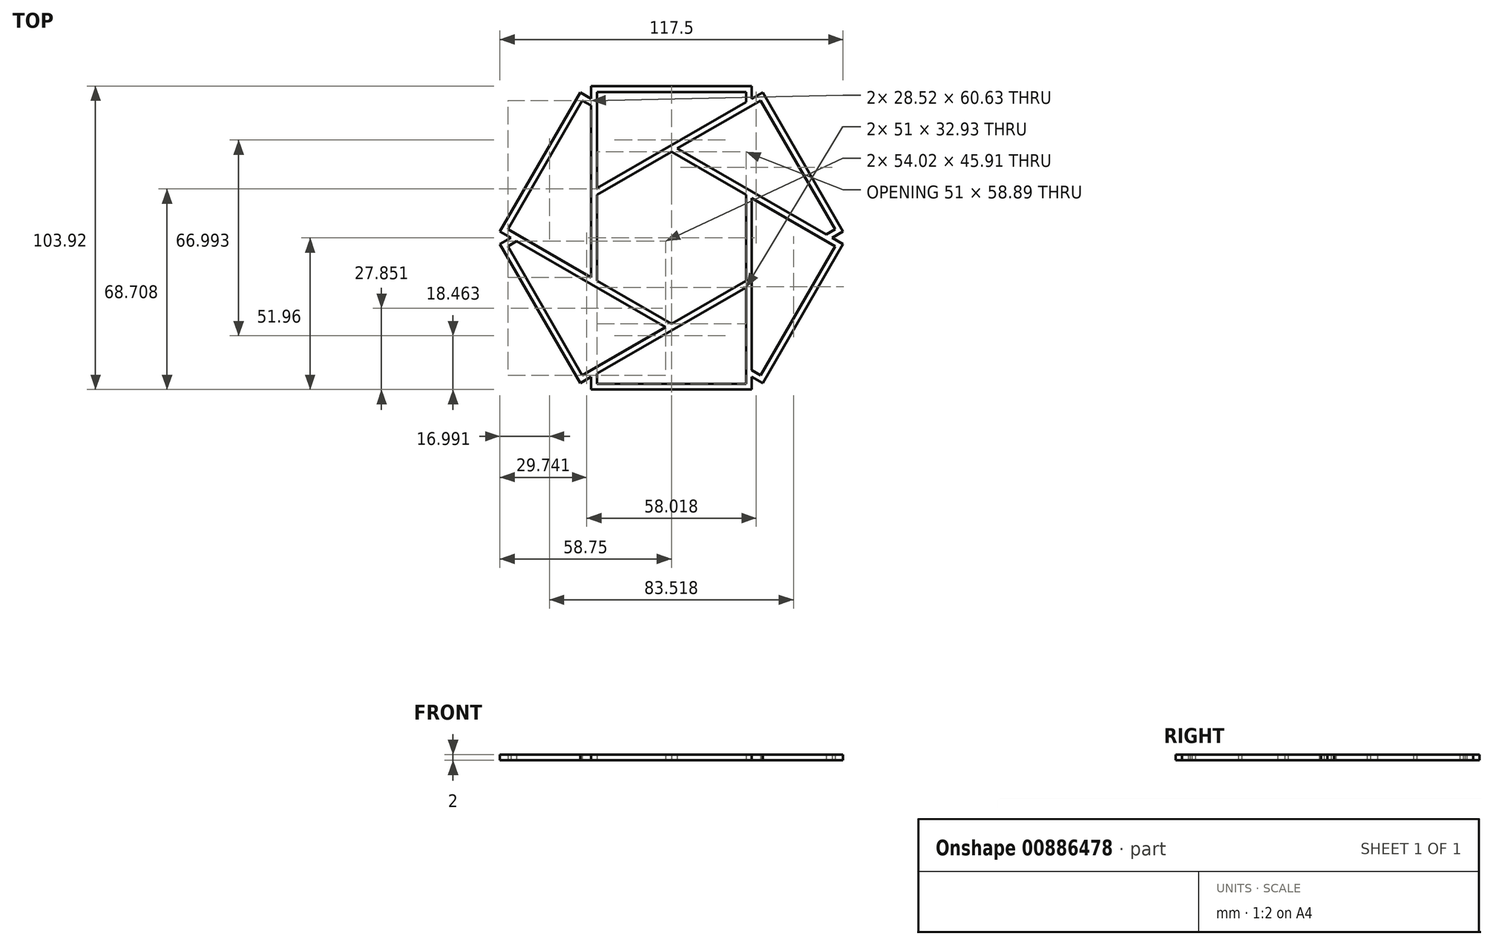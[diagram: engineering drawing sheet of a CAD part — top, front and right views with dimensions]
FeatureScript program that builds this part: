
annotation { "Feature Type Name" : "Feature", "Feature Type Description" : "" }
export const myFeature = defineFeature(function(context is Context, id is Id, definition is map)
    precondition{}
    {
        {
            var Q0;
            Q0=qCreatedBy(makeId("Top.planeOp"),FACE);
            var sketch = newSketch(context, id + "F0", { "sketchPlane" : qUnion([Q0])});
            skCircle(sketch, "E0.cCircle", {"center": v(0, 0) * mm, "radius": 60 * mm, "construction": true});
            skLineSegment(sketch, "E0.0", {"start": v(-60, 0) * mm, "end": v(-30, 51.96) * mm, "construction": true});
            skLineSegment(sketch, "E0.1", {"start": v(-30, 51.96) * mm, "end": v(30, 51.96) * mm, "construction": true});
            skLineSegment(sketch, "E0.2", {"start": v(30, 51.96) * mm, "end": v(60, 0) * mm, "construction": true});
            skLineSegment(sketch, "E0.3", {"start": v(60, 0) * mm, "end": v(30, -51.96) * mm, "construction": true});
            skLineSegment(sketch, "E0.4", {"start": v(30, -51.96) * mm, "end": v(-30, -51.96) * mm, "construction": true});
            skLineSegment(sketch, "E0.5", {"start": v(-30, -51.96) * mm, "end": v(-60, 0) * mm, "construction": true});
            skLineSegment(sketch, "E1.bottom", {"start": v(-27.5, 51.96) * mm, "end": v(27.5, 51.96) * mm});
            skLineSegment(sketch, "E1.top", {"start": v(-27.5, -51.96) * mm, "end": v(27.5, -51.96) * mm});
            skLineSegment(sketch, "E1.left", {"start": v(-27.5, 51.96) * mm, "end": v(-27.5, -15.88) * mm});
            skLineSegment(sketch, "E1.right", {"start": v(27.5, 51.96) * mm, "end": v(27.5, 45.32) * mm});
            skLineSegment(sketch, "E2.0", {"start": v(-25.5, -49.96) * mm, "end": v(25.5, -49.96) * mm});
            skLineSegment(sketch, "E2.1", {"start": v(-25.5, 49.96) * mm, "end": v(-25.5, -17.03) * mm});
            skLineSegment(sketch, "E2.2", {"start": v(-25.5, 49.96) * mm, "end": v(25.5, 49.96) * mm});
            skLineSegment(sketch, "E2.3", {"start": v(25.5, 49.96) * mm, "end": v(25.5, 44.17) * mm});
            skLineSegment(sketch, "E3.1.0", {"start": v(-30.52, -47.06) * mm, "end": v(27.5, -13.57) * mm});
            skLineSegment(sketch, "E3.1.1", {"start": v(58.75, 2.17) * mm, "end": v(31.25, 49.8) * mm});
            skLineSegment(sketch, "E3.1.2", {"start": v(-31.25, -49.8) * mm, "end": v(-58.75, -2.17) * mm});
            skLineSegment(sketch, "E3.1.3", {"start": v(-30.52, -47.06) * mm, "end": v(-56.02, -2.9) * mm});
            skLineSegment(sketch, "E3.1.4", {"start": v(-56.02, -2.9) * mm, "end": v(-51, 0) * mm});
            skLineSegment(sketch, "E3.1.5", {"start": v(-58.75, -2.17) * mm, "end": v(-53, 1.15) * mm});
            skLineSegment(sketch, "E3.1.7", {"start": v(56.02, 2.9) * mm, "end": v(30.52, 47.06) * mm});
            skLineSegment(sketch, "E3.1.8", {"start": v(-31.25, -49.8) * mm, "end": v(27.5, -15.88) * mm});
            skLineSegment(sketch, "E3.2.0", {"start": v(56.02, -2.9) * mm, "end": v(-2, 30.6) * mm});
            skLineSegment(sketch, "E3.2.1", {"start": v(-31.25, 49.8) * mm, "end": v(-58.75, 2.17) * mm});
            skLineSegment(sketch, "E3.2.2", {"start": v(58.75, -2.17) * mm, "end": v(31.25, -49.8) * mm});
            skLineSegment(sketch, "E3.2.3", {"start": v(56.02, -2.9) * mm, "end": v(30.52, -47.06) * mm});
            skLineSegment(sketch, "E3.2.4", {"start": v(30.52, -47.06) * mm, "end": v(25.5, -44.17) * mm});
            skLineSegment(sketch, "E3.2.5", {"start": v(31.25, -49.8) * mm, "end": v(25.5, -46.48) * mm});
            skLineSegment(sketch, "E3.2.7", {"start": v(-30.52, 47.06) * mm, "end": v(-56.02, 2.9) * mm});
            skLineSegment(sketch, "E3.2.8", {"start": v(58.75, -2.17) * mm, "end": v(0, 31.75) * mm});
            skLineSegment(sketch, "E4.trimOffspring", {"start": v(-25.5, 44.17) * mm, "end": v(-30.52, 47.06) * mm});
            skLineSegment(sketch, "E5.trimOffspring", {"start": v(-25.5, 46.48) * mm, "end": v(-31.25, 49.8) * mm});
            skLineSegment(sketch, "E6.trimOffspring", {"start": v(-27.5, 15.88) * mm, "end": v(31.25, 49.8) * mm});
            skLineSegment(sketch, "E7.trimOffspring", {"start": v(-27.5, 13.57) * mm, "end": v(30.52, 47.06) * mm});
            skLineSegment(sketch, "E8.trimOffspring", {"start": v(-27.5, -45.32) * mm, "end": v(-27.5, -51.96) * mm});
            skLineSegment(sketch, "E9.trimOffspring", {"start": v(-25.5, -44.17) * mm, "end": v(-25.5, -49.96) * mm});
            skLineSegment(sketch, "E10.trimOffspring", {"start": v(0, -31.75) * mm, "end": v(-58.75, 2.17) * mm});
            skLineSegment(sketch, "E11.trimOffspring", {"start": v(2, -30.6) * mm, "end": v(-56.02, 2.9) * mm});
            skLineSegment(sketch, "E12.trimOffspring", {"start": v(51, 0) * mm, "end": v(56.02, 2.9) * mm});
            skLineSegment(sketch, "E13.trimOffspring", {"start": v(53, -1.15) * mm, "end": v(58.75, 2.17) * mm});
            skLineSegment(sketch, "E14.trimOffspring", {"start": v(27.5, 15.88) * mm, "end": v(27.5, -51.96) * mm});
            skLineSegment(sketch, "E15.trimOffspring", {"start": v(25.5, 17.03) * mm, "end": v(25.5, -49.96) * mm});
            skSolve(sketch);
        }
        {
            var Q0;
            {var subQ0=sQuery(id+"F0.wireOp",EDGE,"E3.1.4");var subQ1=sQuery(id+"F0.wireOp",EDGE,"E1.left");var subQ2=makeQuery(id+"F0.imprint","INTERSECT",VERTEX,{"derivedFrom":[subQ1,subQ0]});Q0=makeQuery(id+"F0.imprint","IMPRINT",FACE,{"disambiguationData":[TD([[makeQuery(id+"F0.imprint","IMPRINT",EDGE,{"disambiguationData":[TD([[subQ2,-1.0]])],"derivedFrom":subQ1}),1.0]])]});}
            var Q1;
            {var subQ0=sQuery(id+"F0.wireOp",EDGE,"E3.2.4");var subQ1=sQuery(id+"F0.wireOp",EDGE,"E1.left");var subQ2=makeQuery(id+"F0.imprint","INTERSECT",VERTEX,{"derivedFrom":[subQ1,subQ0]});Q1=makeQuery(id+"F0.imprint","IMPRINT",FACE,{"disambiguationData":[TD([[makeQuery(id+"F0.imprint","IMPRINT",EDGE,{"disambiguationData":[TD([[subQ2,-1.0]])],"derivedFrom":subQ1}),1.0]])]});}
            var Q2;
            {var subQ0=sQuery(id+"F0.wireOp",EDGE,"E3.2.5");var subQ1=sQuery(id+"F0.wireOp",EDGE,"E1.left");var subQ2=makeQuery(id+"F0.imprint","INTERSECT",VERTEX,{"derivedFrom":[subQ1,subQ0]});Q2=makeQuery(id+"F0.imprint","IMPRINT",FACE,{"disambiguationData":[TD([[makeQuery(id+"F0.imprint","IMPRINT",EDGE,{"disambiguationData":[TD([[subQ2,-1.0]])],"derivedFrom":subQ1}),1.0]])]});}
            var Q3;
            {var subQ0=sQuery(id+"F0.wireOp",EDGE,"E3.1.8");var subQ1=sQuery(id+"F0.wireOp",EDGE,"E1.left");var subQ2=makeQuery(id+"F0.imprint","INTERSECT",VERTEX,{"derivedFrom":[subQ1,subQ0]});Q3=makeQuery(id+"F0.imprint","IMPRINT",FACE,{"disambiguationData":[TD([[makeQuery(id+"F0.imprint","IMPRINT",EDGE,{"disambiguationData":[TD([[subQ2,1.0]])],"derivedFrom":subQ1}),1.0]])]});}
            var Q4;
            {var subQ4=sQuery(id+"F0.wireOp",EDGE,"E3.1.2");Q4=makeQuery(id+"F0.imprint","IMPRINT",FACE,{"disambiguationData":[TD([[makeQuery(id+"F0.imprint","IMPRINT",EDGE,{"derivedFrom":subQ4}),-1.0]])]});}
            var Q5;
            {var subQ1=sQuery(id+"F0.wireOp",EDGE,"E1.top");Q5=makeQuery(id+"F0.imprint","IMPRINT",FACE,{"disambiguationData":[TD([[makeQuery(id+"F0.imprint","IMPRINT",EDGE,{"derivedFrom":subQ1}),1.0]])]});}
            var Q6;
            {var subQ0=sQuery(id+"F0.wireOp",EDGE,"E3.2.4");var subQ1=sQuery(id+"F0.wireOp",EDGE,"E2.3");var subQ2=makeQuery(id+"F0.imprint","INTERSECT",VERTEX,{"derivedFrom":[subQ1,subQ0]});Q6=makeQuery(id+"F0.imprint","IMPRINT",FACE,{"disambiguationData":[TD([[makeQuery(id+"F0.imprint","IMPRINT",EDGE,{"disambiguationData":[TD([[subQ2,-1.0]])],"derivedFrom":subQ1}),-1.0]])]});}
            var Q7;
            {var subQ0=sQuery(id+"F0.wireOp",EDGE,"E3.2.5");var subQ1=sQuery(id+"F0.wireOp",EDGE,"E1.right");var subQ2=makeQuery(id+"F0.imprint","INTERSECT",VERTEX,{"derivedFrom":[subQ1,subQ0]});Q7=makeQuery(id+"F0.imprint","IMPRINT",FACE,{"disambiguationData":[TD([[makeQuery(id+"F0.imprint","IMPRINT",EDGE,{"disambiguationData":[TD([[subQ2,1.0]])],"derivedFrom":subQ1}),-1.0]])]});}
            var Q8;
            {var subQ0=sQuery(id+"F0.wireOp",EDGE,"E3.2.5");var subQ1=sQuery(id+"F0.wireOp",EDGE,"E3.1.0");var subQ2=makeQuery(id+"F0.imprint","INTERSECT",VERTEX,{"derivedFrom":[subQ1,subQ0]});Q8=makeQuery(id+"F0.imprint","IMPRINT",FACE,{"disambiguationData":[TD([[makeQuery(id+"F0.imprint","IMPRINT",EDGE,{"disambiguationData":[TD([[subQ2,-1.0]])],"derivedFrom":subQ1}),-1.0]])]});}
            var Q9;
            {var subQ0=sQuery(id+"F0.wireOp",EDGE,"E3.1.0");var subQ1=sQuery(id+"F0.wireOp",EDGE,"E2.3");var subQ2=makeQuery(id+"F0.imprint","INTERSECT",VERTEX,{"derivedFrom":[subQ1,subQ0]});Q9=makeQuery(id+"F0.imprint","IMPRINT",FACE,{"disambiguationData":[TD([[makeQuery(id+"F0.imprint","IMPRINT",EDGE,{"disambiguationData":[TD([[subQ2,-1.0]])],"derivedFrom":subQ1}),-1.0]])]});}
            var Q10;
            {var subQ0=sQuery(id+"F0.wireOp",EDGE,"E3.1.8");var subQ1=sQuery(id+"F0.wireOp",EDGE,"E1.right");var subQ2=makeQuery(id+"F0.imprint","INTERSECT",VERTEX,{"derivedFrom":[subQ1,subQ0]});Q10=makeQuery(id+"F0.imprint","IMPRINT",FACE,{"disambiguationData":[TD([[makeQuery(id+"F0.imprint","IMPRINT",EDGE,{"disambiguationData":[TD([[subQ2,-1.0]])],"derivedFrom":subQ1}),-1.0]])]});}
            var Q11;
            {var subQ0=sQuery(id+"F0.wireOp",EDGE,"E3.1.0");var subQ1=sQuery(id+"F0.wireOp",EDGE,"E1.right");var subQ2=makeQuery(id+"F0.imprint","INTERSECT",VERTEX,{"derivedFrom":[subQ1,subQ0]});Q11=makeQuery(id+"F0.imprint","IMPRINT",FACE,{"disambiguationData":[TD([[makeQuery(id+"F0.imprint","IMPRINT",EDGE,{"disambiguationData":[TD([[subQ2,-1.0]])],"derivedFrom":subQ1}),-1.0]])]});}
            var Q12;
            {var subQ0=sQuery(id+"F0.wireOp",EDGE,"E3.2.2");Q12=makeQuery(id+"F0.imprint","IMPRINT",FACE,{"disambiguationData":[TD([[makeQuery(id+"F0.imprint","IMPRINT",EDGE,{"derivedFrom":subQ0}),-1.0]])]});}
            var Q13;
            {var subQ0=sQuery(id+"F0.wireOp",EDGE,"E3.1.0");var subQ1=sQuery(id+"F0.wireOp",EDGE,"E1.right");var subQ2=makeQuery(id+"F0.imprint","INTERSECT",VERTEX,{"derivedFrom":[subQ1,subQ0]});Q13=makeQuery(id+"F0.imprint","IMPRINT",FACE,{"disambiguationData":[TD([[makeQuery(id+"F0.imprint","IMPRINT",EDGE,{"disambiguationData":[TD([[subQ2,-1.0]])],"derivedFrom":subQ1}),1.0]])]});}
            var Q14;
            {var subQ0=sQuery(id+"F0.wireOp",EDGE,"E3.2.5");var subQ1=sQuery(id+"F0.wireOp",EDGE,"E3.1.4");var subQ2=makeQuery(id+"F0.imprint","INTERSECT",VERTEX,{"derivedFrom":[subQ1,subQ0]});Q14=makeQuery(id+"F0.imprint","IMPRINT",FACE,{"disambiguationData":[TD([[makeQuery(id+"F0.imprint","IMPRINT",EDGE,{"disambiguationData":[TD([[subQ2,-1.0]])],"derivedFrom":subQ1}),1.0]])]});}
            var Q15;
            {var subQ0=sQuery(id+"F0.wireOp",EDGE,"E3.2.1");Q15=makeQuery(id+"F0.imprint","IMPRINT",FACE,{"disambiguationData":[TD([[makeQuery(id+"F0.imprint","IMPRINT",EDGE,{"derivedFrom":subQ0}),1.0]])]});}
            var Q16;
            {var subQ0=sQuery(id+"F0.wireOp",EDGE,"E3.2.0");var subQ1=sQuery(id+"F0.wireOp",EDGE,"E1.left");var subQ2=makeQuery(id+"F0.imprint","INTERSECT",VERTEX,{"derivedFrom":[subQ1,subQ0]});Q16=makeQuery(id+"F0.imprint","IMPRINT",FACE,{"disambiguationData":[TD([[makeQuery(id+"F0.imprint","IMPRINT",EDGE,{"disambiguationData":[TD([[subQ2,-1.0]])],"derivedFrom":subQ1}),1.0]])]});}
            var Q17;
            {var subQ0=sQuery(id+"F0.wireOp",EDGE,"E3.1.5");var subQ1=sQuery(id+"F0.wireOp",EDGE,"E1.left");var subQ2=makeQuery(id+"F0.imprint","INTERSECT",VERTEX,{"derivedFrom":[subQ1,subQ0]});Q17=makeQuery(id+"F0.imprint","IMPRINT",FACE,{"disambiguationData":[TD([[makeQuery(id+"F0.imprint","IMPRINT",EDGE,{"disambiguationData":[TD([[subQ2,-1.0]])],"derivedFrom":subQ1}),1.0]])]});}
            var Q18;
            {var subQ0=sQuery(id+"F0.wireOp",EDGE,"E3.2.8");var subQ1=sQuery(id+"F0.wireOp",EDGE,"E1.left");var subQ2=makeQuery(id+"F0.imprint","INTERSECT",VERTEX,{"derivedFrom":[subQ1,subQ0]});Q18=makeQuery(id+"F0.imprint","IMPRINT",FACE,{"disambiguationData":[TD([[makeQuery(id+"F0.imprint","IMPRINT",EDGE,{"disambiguationData":[TD([[subQ2,-1.0]])],"derivedFrom":subQ1}),1.0]])]});}
            var Q19;
            {var subQ5=sQuery(id+"F0.wireOp",EDGE,"E1.bottom");Q19=makeQuery(id+"F0.imprint","IMPRINT",FACE,{"disambiguationData":[TD([[makeQuery(id+"F0.imprint","IMPRINT",EDGE,{"derivedFrom":subQ5}),-1.0]])]});}
            var Q20;
            {var subQ0=sQuery(id+"F0.wireOp",EDGE,"E3.2.0");var subQ1=sQuery(id+"F0.wireOp",EDGE,"E3.1.4");var subQ2=makeQuery(id+"F0.imprint","INTERSECT",VERTEX,{"derivedFrom":[subQ1,subQ0]});Q20=makeQuery(id+"F0.imprint","IMPRINT",FACE,{"disambiguationData":[TD([[makeQuery(id+"F0.imprint","IMPRINT",EDGE,{"disambiguationData":[TD([[subQ2,-1.0]])],"derivedFrom":subQ1}),1.0]])]});}
            var Q21;
            {var subQ0=sQuery(id+"F0.wireOp",EDGE,"E3.1.5");var subQ1=sQuery(id+"F0.wireOp",EDGE,"E2.3");var subQ2=makeQuery(id+"F0.imprint","INTERSECT",VERTEX,{"derivedFrom":[subQ1,subQ0]});Q21=makeQuery(id+"F0.imprint","IMPRINT",FACE,{"disambiguationData":[TD([[makeQuery(id+"F0.imprint","IMPRINT",EDGE,{"disambiguationData":[TD([[subQ2,-1.0]])],"derivedFrom":subQ1}),-1.0]])]});}
            var Q22;
            {var subQ0=sQuery(id+"F0.wireOp",EDGE,"E3.2.8");var subQ1=sQuery(id+"F0.wireOp",EDGE,"E2.3");var subQ2=makeQuery(id+"F0.imprint","INTERSECT",VERTEX,{"derivedFrom":[subQ1,subQ0]});Q22=makeQuery(id+"F0.imprint","IMPRINT",FACE,{"disambiguationData":[TD([[makeQuery(id+"F0.imprint","IMPRINT",EDGE,{"disambiguationData":[TD([[subQ2,-1.0]])],"derivedFrom":subQ1}),-1.0]])]});}
            var Q23;
            {var subQ0=sQuery(id+"F0.wireOp",EDGE,"E3.1.4");var subQ1=sQuery(id+"F0.wireOp",EDGE,"E1.right");var subQ2=makeQuery(id+"F0.imprint","INTERSECT",VERTEX,{"derivedFrom":[subQ1,subQ0]});Q23=makeQuery(id+"F0.imprint","IMPRINT",FACE,{"disambiguationData":[TD([[makeQuery(id+"F0.imprint","IMPRINT",EDGE,{"disambiguationData":[TD([[subQ2,-1.0]])],"derivedFrom":subQ1}),-1.0]])]});}
            var Q24;
            {var subQ0=sQuery(id+"F0.wireOp",EDGE,"E3.1.5");var subQ1=sQuery(id+"F0.wireOp",EDGE,"E1.right");var subQ2=makeQuery(id+"F0.imprint","INTERSECT",VERTEX,{"derivedFrom":[subQ1,subQ0]});Q24=makeQuery(id+"F0.imprint","IMPRINT",FACE,{"disambiguationData":[TD([[makeQuery(id+"F0.imprint","IMPRINT",EDGE,{"disambiguationData":[TD([[subQ2,-1.0]])],"derivedFrom":subQ1}),-1.0]])]});}
            var Q25;
            {var subQ4=sQuery(id+"F0.wireOp",EDGE,"E3.1.1");Q25=makeQuery(id+"F0.imprint","IMPRINT",FACE,{"disambiguationData":[TD([[makeQuery(id+"F0.imprint","IMPRINT",EDGE,{"derivedFrom":subQ4}),1.0]])]});}
            var Q26;
            {var subQ0=sQuery(id+"F0.wireOp",EDGE,"E3.2.8");var subQ1=sQuery(id+"F0.wireOp",EDGE,"E1.right");var subQ2=makeQuery(id+"F0.imprint","INTERSECT",VERTEX,{"derivedFrom":[subQ1,subQ0]});Q26=makeQuery(id+"F0.imprint","IMPRINT",FACE,{"disambiguationData":[TD([[makeQuery(id+"F0.imprint","IMPRINT",EDGE,{"disambiguationData":[TD([[subQ2,-1.0]])],"derivedFrom":subQ1}),-1.0]])]});}
            var Q27;
            {var subQ0=sQuery(id+"F0.wireOp",EDGE,"E3.2.0");var subQ1=sQuery(id+"F0.wireOp",EDGE,"E1.right");var subQ2=makeQuery(id+"F0.imprint","INTERSECT",VERTEX,{"derivedFrom":[subQ1,subQ0]});Q27=makeQuery(id+"F0.imprint","IMPRINT",FACE,{"disambiguationData":[TD([[makeQuery(id+"F0.imprint","IMPRINT",EDGE,{"disambiguationData":[TD([[subQ2,-1.0]])],"derivedFrom":subQ1}),-1.0]])]});}
            var Q28;
            {var subQ0=sQuery(id+"F0.wireOp",EDGE,"E3.2.8");var subQ1=sQuery(id+"F0.wireOp",EDGE,"E1.right");var subQ2=makeQuery(id+"F0.imprint","INTERSECT",VERTEX,{"derivedFrom":[subQ1,subQ0]});Q28=makeQuery(id+"F0.imprint","IMPRINT",FACE,{"disambiguationData":[TD([[makeQuery(id+"F0.imprint","IMPRINT",EDGE,{"disambiguationData":[TD([[subQ2,-1.0]])],"derivedFrom":subQ1}),1.0]])]});}
            var Q29;
            {var subQ0=sQuery(id+"F0.wireOp",EDGE,"E3.2.0");var subQ1=sQuery(id+"F0.wireOp",EDGE,"E3.1.0");var subQ2=makeQuery(id+"F0.imprint","INTERSECT",VERTEX,{"derivedFrom":[subQ1,subQ0]});Q29=makeQuery(id+"F0.imprint","IMPRINT",FACE,{"disambiguationData":[TD([[makeQuery(id+"F0.imprint","IMPRINT",EDGE,{"disambiguationData":[TD([[subQ2,-1.0]])],"derivedFrom":subQ1}),-1.0]])]});}
            var Q30;
            {var subQ0=sQuery(id+"F0.wireOp",EDGE,"E6.trimOffspring");var subQ1=sQuery(id+"F0.wireOp",EDGE,"E2.1");var subQ2=makeQuery(id+"F0.imprint","INTERSECT",VERTEX,{"derivedFrom":[subQ1,subQ0]});Q30=makeQuery(id+"F0.imprint","IMPRINT",FACE,{"disambiguationData":[TD([[makeQuery(id+"F0.imprint","IMPRINT",EDGE,{"disambiguationData":[TD([[subQ2,-1.0]])],"derivedFrom":subQ1}),1.0]])]});}
            var Q31;
            {var subQ0=sQuery(id+"F0.wireOp",EDGE,"E6.trimOffspring");var subQ1=sQuery(id+"F0.wireOp",EDGE,"E3.2.0");var subQ2=makeQuery(id+"F0.imprint","INTERSECT",VERTEX,{"derivedFrom":[subQ1,subQ0]});Q31=makeQuery(id+"F0.imprint","IMPRINT",FACE,{"disambiguationData":[TD([[makeQuery(id+"F0.imprint","IMPRINT",EDGE,{"disambiguationData":[TD([[subQ2,1.0]])],"derivedFrom":subQ1}),-1.0]])]});}
            var Q32;
            {var subQ0=sQuery(id+"F0.wireOp",EDGE,"E12.trimOffspring");var subQ1=sQuery(id+"F0.wireOp",EDGE,"E3.2.0");var subQ2=makeQuery(id+"F0.imprint","INTERSECT",VERTEX,{"derivedFrom":[subQ1,subQ0]});Q32=makeQuery(id+"F0.imprint","IMPRINT",FACE,{"disambiguationData":[TD([[makeQuery(id+"F0.imprint","IMPRINT",EDGE,{"disambiguationData":[TD([[subQ2,1.0]])],"derivedFrom":subQ1}),-1.0]])]});}
            var Q33;
            {var subQ0=sQuery(id+"F0.wireOp",EDGE,"E10.trimOffspring");var subQ1=sQuery(id+"F0.wireOp",EDGE,"E1.left");var subQ2=makeQuery(id+"F0.imprint","INTERSECT",VERTEX,{"derivedFrom":[subQ1,subQ0]});Q33=makeQuery(id+"F0.imprint","IMPRINT",FACE,{"disambiguationData":[TD([[makeQuery(id+"F0.imprint","IMPRINT",EDGE,{"disambiguationData":[TD([[subQ2,1.0]])],"derivedFrom":subQ1}),-1.0]])]});}
            var Q34;
            {var subQ0=sQuery(id+"F0.wireOp",EDGE,"E10.trimOffspring");var subQ1=sQuery(id+"F0.wireOp",EDGE,"E2.1");var subQ2=makeQuery(id+"F0.imprint","INTERSECT",VERTEX,{"derivedFrom":[subQ1,subQ0]});Q34=makeQuery(id+"F0.imprint","IMPRINT",FACE,{"disambiguationData":[TD([[makeQuery(id+"F0.imprint","IMPRINT",EDGE,{"disambiguationData":[TD([[subQ2,1.0]])],"derivedFrom":subQ1}),1.0]])]});}
            var Q35;
            {var subQ0=sQuery(id+"F0.wireOp",EDGE,"E14.trimOffspring");var subQ1=sQuery(id+"F0.wireOp",EDGE,"E3.1.0");var subQ2=makeQuery(id+"F0.imprint","INTERSECT",VERTEX,{"derivedFrom":[subQ1,subQ0]});Q35=makeQuery(id+"F0.imprint","IMPRINT",FACE,{"disambiguationData":[TD([[makeQuery(id+"F0.imprint","IMPRINT",EDGE,{"disambiguationData":[TD([[subQ2,1.0]])],"derivedFrom":subQ1}),1.0]])]});}
            var Q36;
            {var subQ0=sQuery(id+"F0.wireOp",EDGE,"E15.trimOffspring");var subQ1=sQuery(id+"F0.wireOp",EDGE,"E3.2.0");var subQ2=makeQuery(id+"F0.imprint","INTERSECT",VERTEX,{"derivedFrom":[subQ1,subQ0]});Q36=makeQuery(id+"F0.imprint","IMPRINT",FACE,{"disambiguationData":[TD([[makeQuery(id+"F0.imprint","IMPRINT",EDGE,{"disambiguationData":[TD([[subQ2,-1.0]])],"derivedFrom":subQ1}),-1.0]])]});}
            var Q37;
            {var subQ0=sQuery(id+"F0.wireOp",EDGE,"E12.trimOffspring");var subQ1=sQuery(id+"F0.wireOp",EDGE,"E3.2.0");var subQ2=makeQuery(id+"F0.imprint","INTERSECT",VERTEX,{"derivedFrom":[subQ1,subQ0]});Q37=makeQuery(id+"F0.imprint","IMPRINT",FACE,{"disambiguationData":[TD([[makeQuery(id+"F0.imprint","IMPRINT",EDGE,{"disambiguationData":[TD([[subQ2,-1.0]])],"derivedFrom":subQ1}),-1.0]])]});}
            var Q38;
            {var subQ0=sQuery(id+"F0.wireOp",EDGE,"E14.trimOffspring");var subQ1=sQuery(id+"F0.wireOp",EDGE,"E3.2.0");var subQ2=makeQuery(id+"F0.imprint","INTERSECT",VERTEX,{"derivedFrom":[subQ1,subQ0]});Q38=makeQuery(id+"F0.imprint","IMPRINT",FACE,{"disambiguationData":[TD([[makeQuery(id+"F0.imprint","IMPRINT",EDGE,{"disambiguationData":[TD([[subQ2,-1.0]])],"derivedFrom":subQ1}),-1.0]])]});}
            var Q39;
            {var subQ0=sQuery(id+"F0.wireOp",EDGE,"E14.trimOffspring");var subQ1=sQuery(id+"F0.wireOp",EDGE,"E3.1.8");var subQ2=makeQuery(id+"F0.imprint","INTERSECT",VERTEX,{"derivedFrom":[subQ1,subQ0]});Q39=makeQuery(id+"F0.imprint","IMPRINT",FACE,{"disambiguationData":[TD([[makeQuery(id+"F0.imprint","IMPRINT",EDGE,{"disambiguationData":[TD([[subQ2,1.0]])],"derivedFrom":subQ1}),-1.0]])]});}
            var Q40;
            {var subQ0=sQuery(id+"F0.wireOp",EDGE,"E15.trimOffspring");var subQ1=sQuery(id+"F0.wireOp",EDGE,"E3.2.4");var subQ2=makeQuery(id+"F0.imprint","INTERSECT",VERTEX,{"derivedFrom":[subQ1,subQ0]});Q40=makeQuery(id+"F0.imprint","IMPRINT",FACE,{"disambiguationData":[TD([[makeQuery(id+"F0.imprint","IMPRINT",EDGE,{"disambiguationData":[TD([[subQ2,1.0]])],"derivedFrom":subQ1}),1.0]])]});}
            extrude(context, id + "F1", {"entities" : qUnion([Q0, Q1, Q2, Q3, Q4, Q5, Q6, Q7, Q8, Q9, Q10, Q11, Q12, Q13, Q14, Q15, Q16, Q17, Q18, Q19, Q20, Q21, Q22, Q23, Q24, Q25, Q26, Q27, Q28, Q29, Q30, Q31, Q32, Q33, Q34, Q35, Q36, Q37, Q38, Q39, Q40]), "depth" : 2 * mm, "offsetDistance" : 25 * mm});
        }
    });
